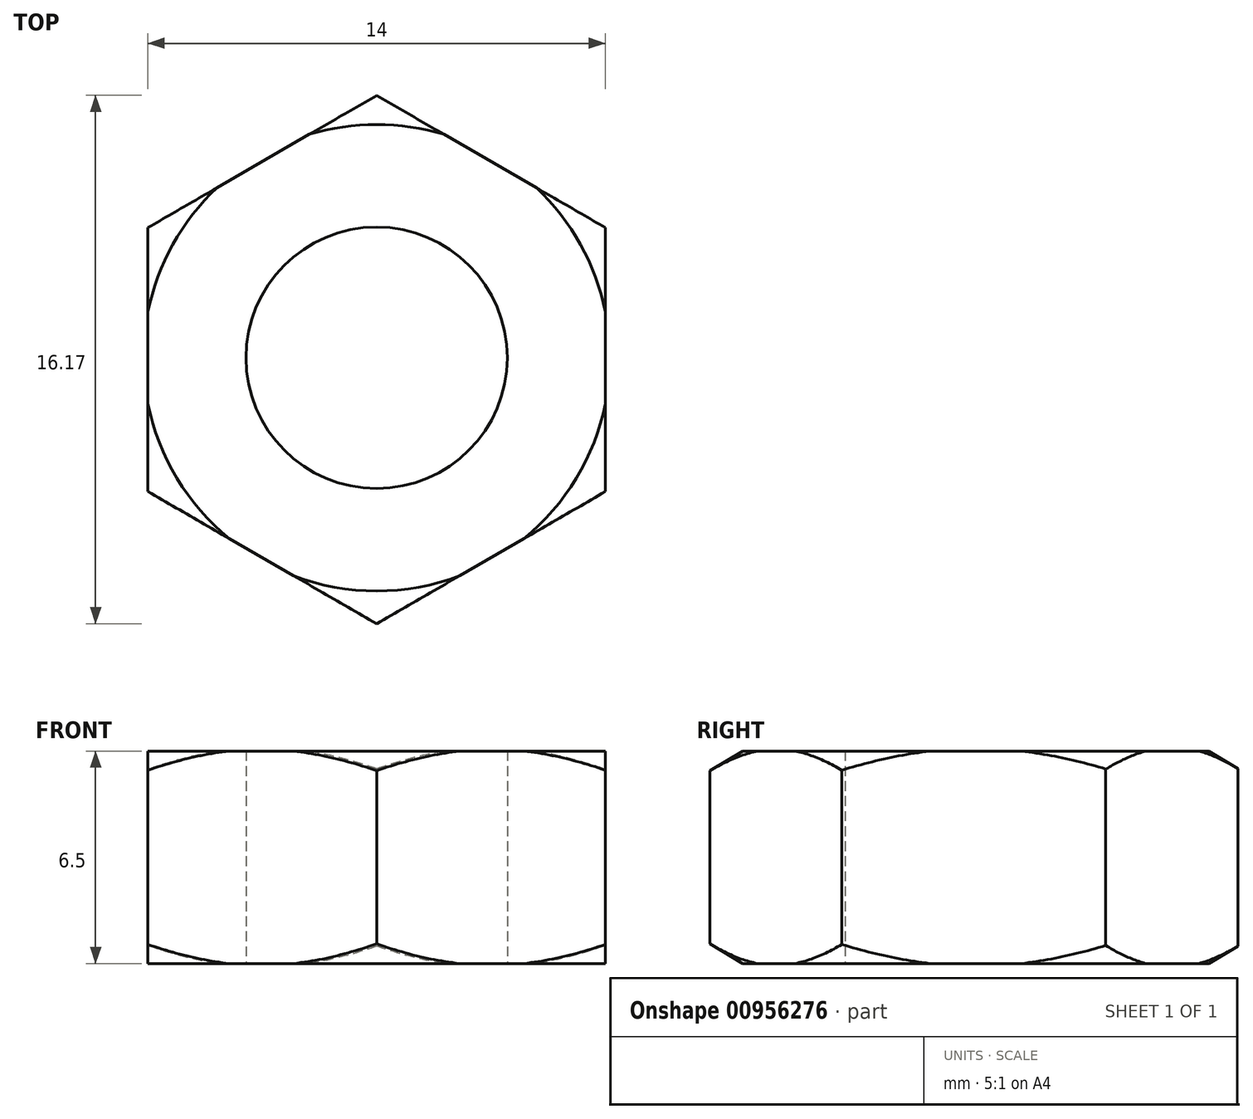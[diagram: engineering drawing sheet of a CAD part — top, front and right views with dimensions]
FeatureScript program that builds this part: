
annotation { "Feature Type Name" : "Feature", "Feature Type Description" : "" }
export const myFeature = defineFeature(function(context is Context, id is Id, definition is map)
    precondition{}
    {
        {
            var Q0;
            Q0=qCreatedBy(makeId("Top.planeOp"),FACE);
            var sketch = newSketch(context, id + "F0", { "sketchPlane" : qUnion([Q0])});
            skCircle(sketch, "E0", {"center": v(0, 0) * mm, "radius": 4 * mm});
            skSolve(sketch);
        }
        {
            var Q0;
            Q0=qSketchRegion(id+"F0",true);
            extrude(context, id + "F1", {"entities" : qUnion([Q0]), "oppositeDirection" : true, "depth" : 15 * mm, "offsetDistance" : 25 * mm});
        }
        {
            var Q0;
            Q0=qCreatedBy(makeId("Top.planeOp"),FACE);
            var sketch = newSketch(context, id + "F2", { "sketchPlane" : qUnion([Q0])});
            skLineSegment(sketch, "E1", {"start": v(0, 8.03) * mm, "end": v(-7, 3.98) * mm});
            skLineSegment(sketch, "E2", {"start": v(-7, 3.98) * mm, "end": v(-7, -4.1) * mm});
            skLineSegment(sketch, "E3", {"start": v(-7, -4.1) * mm, "end": v(0, -8.14) * mm});
            skLineSegment(sketch, "E4", {"start": v(0, -8.14) * mm, "end": v(7, -4.1) * mm});
            skLineSegment(sketch, "E5", {"start": v(7, -4.1) * mm, "end": v(7, 3.98) * mm});
            skLineSegment(sketch, "E6", {"start": v(7, 3.98) * mm, "end": v(0, 8.03) * mm});
            skSolve(sketch);
        }
        {
            var Q0;
            Q0=qSketchRegion(id+"F2",true);
            extrude(context, id + "F3", {"entities" : qUnion([Q0]), "operationType" : NewBodyOperationType.ADD, "depth" : 6.5 * mm, "offsetDistance" : 25 * mm});
        }
        {
            var Q0;
            Q0=qCreatedBy(makeId("Right.planeOp"),FACE);
            var sketch = newSketch(context, id + "F4", { "sketchPlane" : qUnion([Q0])});
            skLineSegment(sketch, "E7", {"start": v(-7.14, 6.5) * mm, "end": v(-8.14, 6.5) * mm});
            skLineSegment(sketch, "E8", {"start": v(-8.14, 6.5) * mm, "end": v(-8.14, 5.9) * mm});
            skLineSegment(sketch, "E9", {"start": v(-8.14, 5.9) * mm, "end": v(-7.14, 6.5) * mm});
            skLineSegment(sketch, "E10", {"start": v(-8.14, 0.6) * mm, "end": v(-7.14, 0) * mm});
            skLineSegment(sketch, "E11", {"start": v(-7.14, 0) * mm, "end": v(-8.14, 0) * mm});
            skLineSegment(sketch, "E12", {"start": v(-8.14, 0) * mm, "end": v(-8.14, 0.6) * mm});
            skSolve(sketch);
        }
        {
            var Q0;
            Q0=makeQuery(id+"F3.opExtrude","CAP_FACE",FACE,{"disambiguationData":[OSD([sQuery(id+"F2.wireOp",EDGE,"E1"),sQuery(id+"F2.wireOp",EDGE,"E2"),sQuery(id+"F2.wireOp",EDGE,"E3"),sQuery(id+"F2.wireOp",EDGE,"E4"),sQuery(id+"F2.wireOp",EDGE,"E5"),sQuery(id+"F2.wireOp",EDGE,"E6")])],"isStart":false});
            var sketch = newSketch(context, id + "F5", { "sketchPlane" : qUnion([Q0])});
            skCircle(sketch, "E13", {"center": v(0, 0) * mm, "radius": 8.14 * mm});
            skSolve(sketch);
        }
        {
            var Q0;
            Q0=qSketchRegion(id+"F4",true);
            var Q1;
            Q1=sQuery(id+"F5.wireOp",EDGE,"E13");
            sweep(context, id + "F6", {"operationType" : NewBodyOperationType.REMOVE, "profiles" : qUnion([Q0]), "path" : qUnion([Q1])});
        }
        {
            var Q0;
            Q0=makeQuery(id+"F1.opExtrude","CAP_FACE",FACE,{"disambiguationData":[OSD([sQuery(id+"F0.wireOp",EDGE,"E0")])],"isStart":false});
            var sketch = newSketch(context, id + "F7", { "sketchPlane" : qUnion([Q0])});
            skCircle(sketch, "E14", {"center": v(0, 0) * mm, "radius": 4 * mm});
            skSolve(sketch);
        }
        {
            var Q0;
            Q0 = qSketchRegion(id + "F7", true);
            var Q1;
            Q1=makeQuery(id+"F3.opExtrude","CAP_FACE",FACE,{"disambiguationData":[OSD([sQuery(id+"F2.wireOp",EDGE,"E1"),sQuery(id+"F2.wireOp",EDGE,"E2"),sQuery(id+"F2.wireOp",EDGE,"E3"),sQuery(id+"F2.wireOp",EDGE,"E4"),sQuery(id+"F2.wireOp",EDGE,"E5"),sQuery(id+"F2.wireOp",EDGE,"E6")])],"isStart":false});
            extrude(context, id + "F8", {"entities" : qUnion([Q0]), "operationType" : NewBodyOperationType.REMOVE, "endBound" : BoundingType.UP_TO_SURFACE, "oppositeDirection" : true, "depth" : 25 * mm, "endBoundEntityFace" : qUnion([Q1]), "offsetDistance" : 25 * mm});
        }
    });
